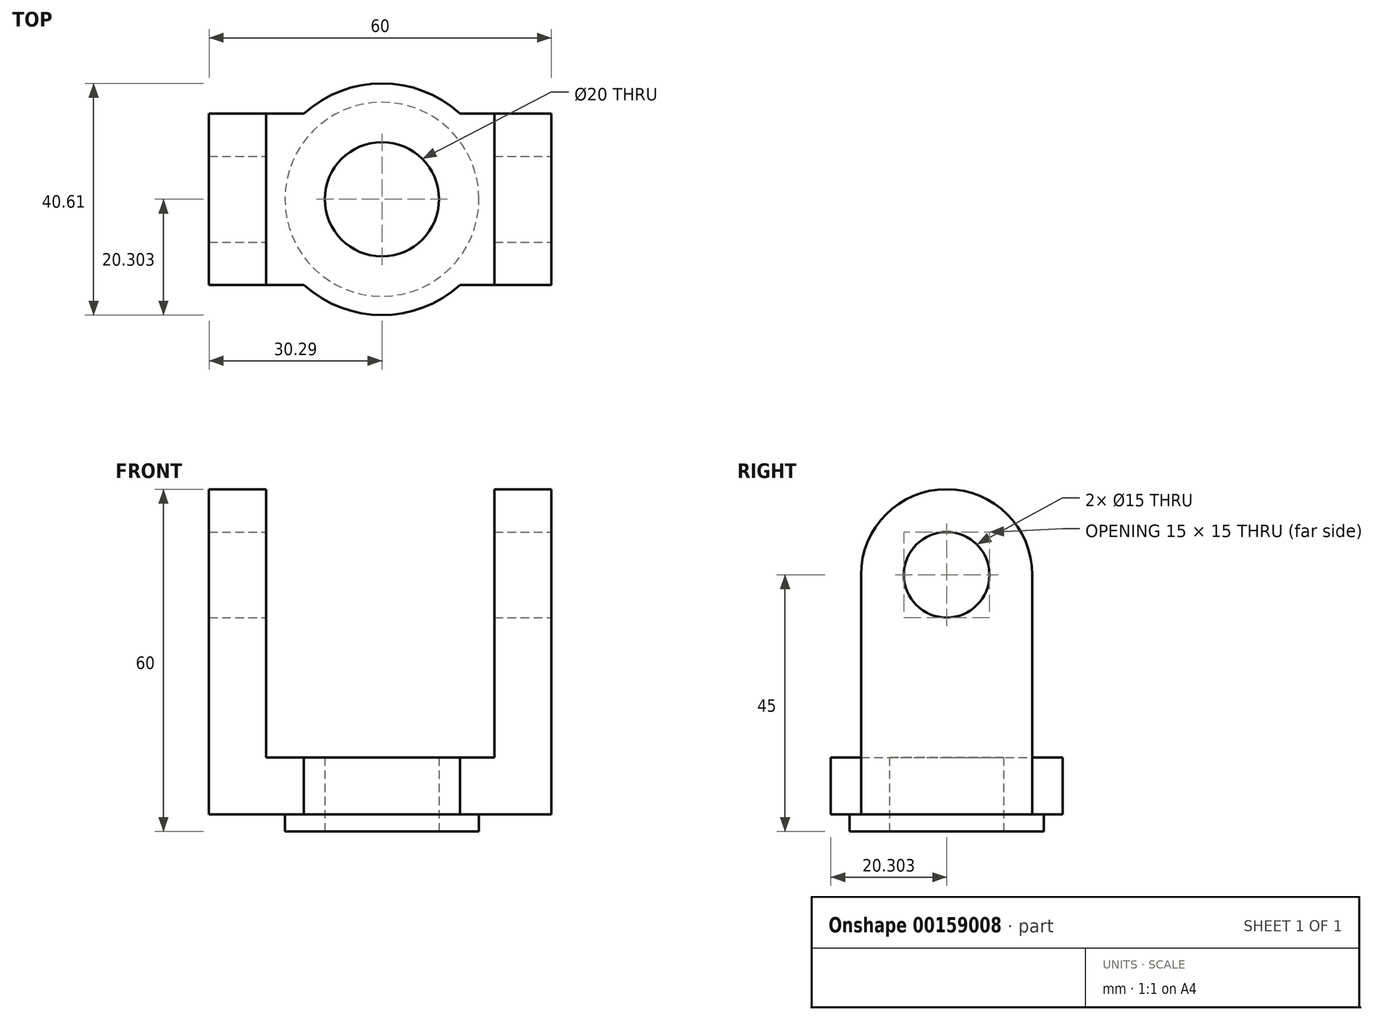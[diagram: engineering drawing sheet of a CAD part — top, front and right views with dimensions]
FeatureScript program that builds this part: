
annotation { "Feature Type Name" : "Feature", "Feature Type Description" : "" }
export const myFeature = defineFeature(function(context is Context, id is Id, definition is map)
    precondition{}
    {
        {
            var Q0;
            Q0=qCreatedBy(makeId("Top.planeOp"),FACE);
            var sketch = newSketch(context, id + "F0", { "sketchPlane" : qUnion([Q0])});
            skLineSegment(sketch, "E0.bottom", {"start": v(-30.3, 24.98) * mm, "end": v(29.7, 24.98) * mm});
            skLineSegment(sketch, "E0.top", {"start": v(-30.3, -5.02) * mm, "end": v(29.7, -5.02) * mm});
            skLineSegment(sketch, "E0.left", {"start": v(-30.3, 24.98) * mm, "end": v(-30.3, -5.02) * mm});
            skLineSegment(sketch, "E0.right", {"start": v(29.7, 24.98) * mm, "end": v(29.7, -5.02) * mm});
            skSolve(sketch);
        }
        {
            var Q0;
            Q0 = qSketchRegion(id + "F0", true);
            extrude(context, id + "F1", {"entities" : qUnion([Q0]), "depth" : 10 * mm});
        }
        {
            var Q0;
            Q0=qCreatedBy(makeId("Top.planeOp"),FACE);
            var sketch = newSketch(context, id + "F2", { "sketchPlane" : qUnion([Q0])});
            skLineSegment(sketch, "E1.0", {"start": v(-30.3, 24.98) * mm, "end": v(29.7, 24.98) * mm});
            skLineSegment(sketch, "E2.0", {"start": v(-30.3, -5.02) * mm, "end": v(29.7, -5.02) * mm});
            skCircle(sketch, "E3", {"center": v(0, 9.98) * mm, "radius": 10 * mm});
            skLineSegment(sketch, "E4", {"start": v(0, 9.98) * mm, "end": v(0, 24.98) * mm, "construction": true});
            skLineSegment(sketch, "E5", {"start": v(0, 9.98) * mm, "end": v(0, -5.02) * mm, "construction": true});
            skArc(sketch, "E6", {"start": v(20.3, 10.53) * mm, "mid": v(0.43, 30.29) * mm, "end": v(-20.26, 11.38) * mm});
            skArc(sketch, "E7", {"start": v(-20.26, 11.38) * mm, "mid": v(-0.43, -10.32) * mm, "end": v(20.3, 10.53) * mm});
            skSolve(sketch);
        }
        {
            var Q0;
            Q0 = qSketchRegion(id + "F2", true);
            extrude(context, id + "F3", {"entities" : qUnion([Q0]), "operationType" : NewBodyOperationType.ADD, "depth" : 10 * mm});
        }
        {
            var Q0;
            Q0=qCreatedBy(makeId("Top.planeOp"),FACE);
            var sketch = newSketch(context, id + "F4", { "sketchPlane" : qUnion([Q0])});
            skCircle(sketch, "E8.0", {"center": v(0, 9.98) * mm, "radius": 10 * mm});
            skSolve(sketch);
        }
        {
            var Q0;
            Q0 = qSketchRegion(id + "F4", true);
            extrude(context, id + "F5", {"entities" : qUnion([Q0]), "operationType" : NewBodyOperationType.REMOVE, "depth" : 10 * mm, "hasSecondDirection" : true, "secondDirectionOppositeDirection" : true, "secondDirectionDepth" : 17.75 * mm});
        }
        {
            var Q0;
            Q0=qCreatedBy(makeId("Top.planeOp"),FACE);
            var sketch = newSketch(context, id + "F6", { "sketchPlane" : qUnion([Q0])});
            skPoint(sketch, "E9.0", {"position": v(0, 9.98) * mm});
            skCircle(sketch, "E10", {"center": v(0, 9.98) * mm, "radius": 17 * mm});
            skSolve(sketch);
        }
        {
            var Q0;
            Q0 = qSketchRegion(id + "F6", true);
            extrude(context, id + "F7", {"entities" : qUnion([Q0]), "operationType" : NewBodyOperationType.ADD, "oppositeDirection" : true, "depth" : 3 * mm});
        }
        {
            var Q0;
            Q0=qCreatedBy(makeId("Top.planeOp"),FACE);
            var sketch = newSketch(context, id + "F8", { "sketchPlane" : qUnion([Q0])});
            skCircle(sketch, "E11.0", {"center": v(0, 9.98) * mm, "radius": 10 * mm});
            skSolve(sketch);
        }
        {
            var Q0;
            Q0 = qSketchRegion(id + "F8", true);
            extrude(context, id + "F9", {"entities" : qUnion([Q0]), "operationType" : NewBodyOperationType.REMOVE, "oppositeDirection" : true, "depth" : 25 * mm});
        }
        {
            var Q0;
            Q0=qCreatedBy(makeId("Front.planeOp"),FACE);
            var sketch = newSketch(context, id + "F10", { "sketchPlane" : qUnion([Q0])});
            skLineSegment(sketch, "E12.0", {"start": v(-30.3, 10) * mm, "end": v(-13.69, 10) * mm});
            skLineSegment(sketch, "E12.1", {"start": v(13.69, 10) * mm, "end": v(29.7, 10) * mm});
            skLineSegment(sketch, "E13.bottom", {"start": v(-30.3, 10) * mm, "end": v(-20.3, 10) * mm});
            skLineSegment(sketch, "E13.top", {"start": v(-30.3, 42) * mm, "end": v(-20.3, 42) * mm});
            skLineSegment(sketch, "E13.left", {"start": v(-30.3, 10) * mm, "end": v(-30.3, 42) * mm});
            skLineSegment(sketch, "E13.right", {"start": v(-20.3, 10) * mm, "end": v(-20.3, 42) * mm});
            skLineSegment(sketch, "E14.bottom", {"start": v(29.7, 10) * mm, "end": v(19.7, 10) * mm});
            skLineSegment(sketch, "E14.top", {"start": v(29.7, 42) * mm, "end": v(19.7, 42) * mm});
            skLineSegment(sketch, "E14.right", {"start": v(19.7, 10) * mm, "end": v(19.7, 42) * mm});
            skLineSegment(sketch, "E15", {"start": v(29.7, 42) * mm, "end": v(29.7, 10) * mm});
            skSolve(sketch);
        }
        {
            var Q0;
            Q0 = qSketchRegion(id + "F10", true);
            var Q1;
            {var subQ0=sQuery(id+"F0.wireOp",EDGE,"E0.right");var subQ2=sQuery(id+"F0.wireOp",EDGE,"E0.top");Q1=makeQuery(id+"F3.boolean.opBoolean","SPLIT",FACE,{"disambiguationData":[TD([makeQuery(id+"F1.opExtrude","SWEPT_FACE",FACE,{"disambiguationData":[OSD([subQ0])]})])],"derivedFrom":makeQuery(id+"F1.opExtrude","SWEPT_FACE",FACE,{"disambiguationData":[OSD([subQ2])]})});}
            var Q2;
            {var subQ0=sQuery(id+"F0.wireOp",EDGE,"E0.right");var subQ3=sQuery(id+"F0.wireOp",EDGE,"E0.bottom");Q2=makeQuery(id+"F3.boolean.opBoolean","SPLIT",FACE,{"disambiguationData":[TD([makeQuery(id+"F1.opExtrude","SWEPT_FACE",FACE,{"disambiguationData":[OSD([subQ0])]})])],"derivedFrom":makeQuery(id+"F1.opExtrude","SWEPT_FACE",FACE,{"disambiguationData":[OSD([subQ3])]})});}
            extrude(context, id + "F11", {"entities" : qUnion([Q0]), "operationType" : NewBodyOperationType.ADD, "endBound" : BoundingType.UP_TO_SURFACE, "endBoundEntityFace" : qUnion([Q1]), "depth" : 25 * mm, "hasSecondDirection" : true, "secondDirectionBound" : SecondDirectionBoundingType.UP_TO_SURFACE, "secondDirectionOppositeDirection" : true, "secondDirectionBoundEntityFace" : qUnion([Q2]), "secondDirectionDepth" : 25 * mm});
        }
        {
            var Q0;
            Q0=qCreatedBy(makeId("Right.planeOp"),FACE);
            var sketch = newSketch(context, id + "F12", { "sketchPlane" : qUnion([Q0])});
            skLineSegment(sketch, "E16.0", {"start": v(-5.02, 42) * mm, "end": v(24.98, 42) * mm});
            skArc(sketch, "E17", {"start": v(24.98, 42) * mm, "mid": v(9.98, 57) * mm, "end": v(-5.02, 42) * mm});
            skSolve(sketch);
        }
        {
            var Q0;
            Q0 = qSketchRegion(id + "F12", true);
            var Q1;
            Q1=makeQuery(id+"F11.boolean.opBoolean","MERGE",FACE,{"derivedFrom":[makeQuery(id+"F1.opExtrude","SWEPT_FACE",FACE,{"disambiguationData":[OSD([sQuery(id+"F0.wireOp",EDGE,"E0.right")])]}),makeQuery(id+"F11.opExtrude","SWEPT_FACE",FACE,{"disambiguationData":[OSD([sQuery(id+"F10.wireOp",EDGE,"E15")])]})]});
            var Q2;
            Q2=makeQuery(id+"F11.opExtrude","SWEPT_FACE",FACE,{"disambiguationData":[OSD([sQuery(id+"F10.wireOp",EDGE,"E14.right")])]});
            extrude(context, id + "F13", {"entities" : qUnion([Q0]), "operationType" : NewBodyOperationType.ADD, "endBound" : BoundingType.UP_TO_SURFACE, "endBoundEntityFace" : qUnion([Q1]), "depth" : 25 * mm, "hasSecondDirection" : true, "secondDirectionBound" : SecondDirectionBoundingType.UP_TO_SURFACE, "secondDirectionOppositeDirection" : false, "secondDirectionBoundEntityFace" : qUnion([Q2]), "secondDirectionDepth" : 25 * mm});
        }
        {
            var Q0;
            Q0 = qSketchRegion(id + "F12", true);
            var Q1;
            Q1=makeQuery(id+"F11.boolean.opBoolean","MERGE",FACE,{"derivedFrom":[makeQuery(id+"F1.opExtrude","SWEPT_FACE",FACE,{"disambiguationData":[OSD([sQuery(id+"F0.wireOp",EDGE,"E0.left")])]}),makeQuery(id+"F11.opExtrude","SWEPT_FACE",FACE,{"disambiguationData":[OSD([sQuery(id+"F10.wireOp",EDGE,"E13.left")])]})]});
            var Q2;
            Q2=makeQuery(id+"F11.opExtrude","SWEPT_FACE",FACE,{"disambiguationData":[OSD([sQuery(id+"F10.wireOp",EDGE,"E13.right")])]});
            extrude(context, id + "F14", {"entities" : qUnion([Q0]), "operationType" : NewBodyOperationType.ADD, "endBound" : BoundingType.UP_TO_SURFACE, "oppositeDirection" : true, "endBoundEntityFace" : qUnion([Q1]), "depth" : 25 * mm, "hasSecondDirection" : true, "secondDirectionBound" : SecondDirectionBoundingType.UP_TO_SURFACE, "secondDirectionOppositeDirection" : true, "secondDirectionBoundEntityFace" : qUnion([Q2]), "secondDirectionDepth" : 25 * mm});
        }
        {
            var Q0;
            Q0=qCreatedBy(makeId("Right.planeOp"),FACE);
            var sketch = newSketch(context, id + "F15", { "sketchPlane" : qUnion([Q0])});
            skPoint(sketch, "E18.0", {"position": v(9.98, 42) * mm});
            skCircle(sketch, "E19", {"center": v(9.98, 42) * mm, "radius": 7.5 * mm});
            skSolve(sketch);
        }
        {
            var Q0;
            Q0 = qSketchRegion(id + "F15", true);
            extrude(context, id + "F16", {"entities" : qUnion([Q0]), "operationType" : NewBodyOperationType.REMOVE, "oppositeDirection" : true, "depth" : 44.75 * mm, "hasSecondDirection" : true, "secondDirectionOppositeDirection" : false, "secondDirectionDepth" : 50.75 * mm});
        }
    });
